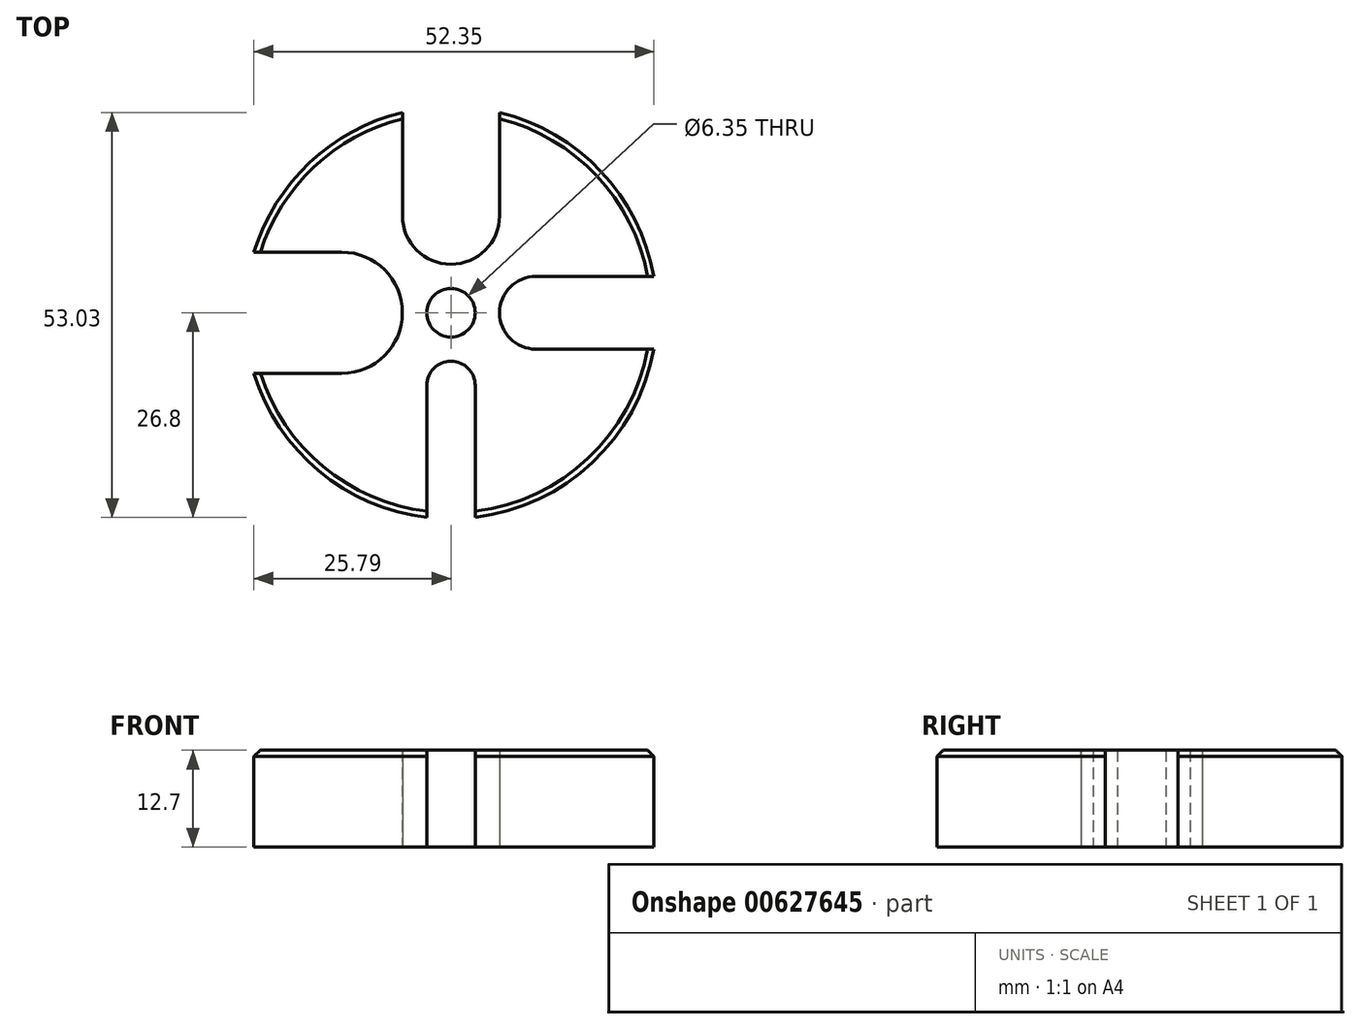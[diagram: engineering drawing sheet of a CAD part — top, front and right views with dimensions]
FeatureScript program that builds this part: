
annotation { "Feature Type Name" : "Feature", "Feature Type Description" : "" }
export const myFeature = defineFeature(function(context is Context, id is Id, definition is map)
    precondition{}
    {
        {
            var Q0;
            Q0=qCreatedBy(makeId("Top.planeOp"),FACE);
            var sketch = newSketch(context, id + "F0", { "sketchPlane" : qUnion([Q0])});
            skArc(sketch, "E0", {"start": v(-6.35, 26.23) * mm, "mid": v(-18.5, 19.66) * mm, "end": v(-25.8, 7.94) * mm});
            skArc(sketch, "E1", {"start": v(-6.35, 12.7) * mm, "mid": v(0, 6.35) * mm, "end": v(6.35, 12.7) * mm});
            skArc(sketch, "E2", {"start": v(11.13, 4.76) * mm, "mid": v(6.36, 0) * mm, "end": v(11.13, -4.76) * mm});
            skArc(sketch, "E3", {"start": v(3.18, -9.53) * mm, "mid": v(0, -6.35) * mm, "end": v(-3.18, -9.53) * mm});
            skArc(sketch, "E4", {"start": v(-14.3, -7.94) * mm, "mid": v(-6.36, 0) * mm, "end": v(-14.3, 7.94) * mm});
            skLineSegment(sketch, "E5", {"start": v(-6.35, 12.7) * mm, "end": v(-6.35, 26.23) * mm});
            skLineSegment(sketch, "E6", {"start": v(6.35, 12.7) * mm, "end": v(6.35, 26.23) * mm});
            skLineSegment(sketch, "E7", {"start": v(11.13, 4.76) * mm, "end": v(26.56, 4.76) * mm});
            skLineSegment(sketch, "E8", {"start": v(11.13, -4.76) * mm, "end": v(26.56, -4.76) * mm});
            skArc(sketch, "E9.trimOffspring", {"start": v(26.56, 4.76) * mm, "mid": v(19.65, 18.5) * mm, "end": v(6.35, 26.23) * mm});
            skLineSegment(sketch, "E10", {"start": v(-3.18, -9.53) * mm, "end": v(-3.18, -26.8) * mm});
            skLineSegment(sketch, "E11", {"start": v(3.18, -9.53) * mm, "end": v(3.17, -26.8) * mm});
            skArc(sketch, "E12.trimOffspring", {"start": v(3.17, -26.8) * mm, "mid": v(18.5, -19.64) * mm, "end": v(26.56, -4.76) * mm});
            skLineSegment(sketch, "E13", {"start": v(-14.3, 7.94) * mm, "end": v(-25.8, 7.94) * mm});
            skLineSegment(sketch, "E14", {"start": v(-14.3, -7.94) * mm, "end": v(-25.8, -7.94) * mm});
            skArc(sketch, "E15.trimOffspring", {"start": v(-25.8, -7.94) * mm, "mid": v(-17.28, -20.73) * mm, "end": v(-3.17, -26.8) * mm});
            skCircle(sketch, "E16", {"center": v(0, 0) * mm, "radius": 3.18 * mm});
            skSolve(sketch);
        }
        {
            var Q0;
            Q0 = qSketchRegion(id + "F0", true);
            extrude(context, id + "F1", {"entities" : qUnion([Q0]), "depth" : 12.7 * mm, "offsetDistance" : 25.4 * mm});
        }
        {
            var Q0;
            Q0=makeQuery(id+"F1.opExtrude","CAP_EDGE",EDGE,{"disambiguationData":[OSD([sQuery(id+"F0.wireOp",EDGE,"E15.trimOffspring")])],"isStart":false});
            var Q1;
            Q1=makeQuery(id+"F1.opExtrude","CAP_EDGE",EDGE,{"disambiguationData":[OSD([sQuery(id+"F0.wireOp",EDGE,"E12.trimOffspring")])],"isStart":false});
            var Q2;
            Q2=makeQuery(id+"F1.opExtrude","CAP_EDGE",EDGE,{"disambiguationData":[OSD([sQuery(id+"F0.wireOp",EDGE,"E9.trimOffspring")])],"isStart":false});
            var Q3;
            Q3=makeQuery(id+"F1.opExtrude","CAP_EDGE",EDGE,{"disambiguationData":[OSD([sQuery(id+"F0.wireOp",EDGE,"E0")])],"isStart":false});
            chamfer(context, id + "F2", {"entities" : qUnion([Q0, Q1, Q2, Q3]), "width" : 0.8 * mm, "tangentPropagation" : true});
        }
    });
